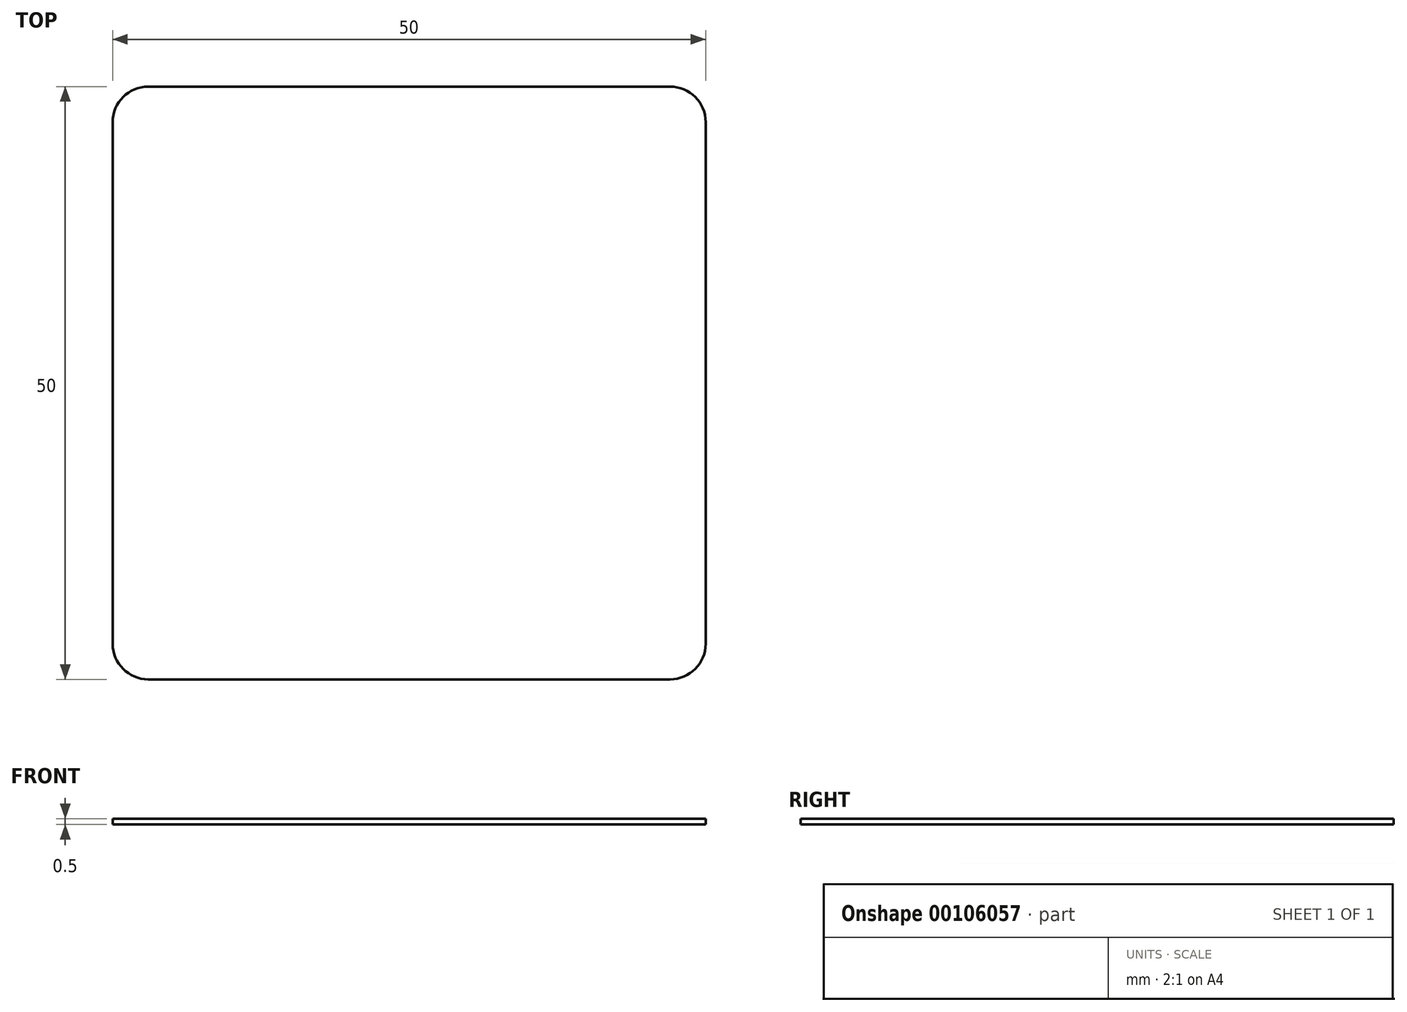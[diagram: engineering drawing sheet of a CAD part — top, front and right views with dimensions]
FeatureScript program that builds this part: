
annotation { "Feature Type Name" : "Feature", "Feature Type Description" : "" }
export const myFeature = defineFeature(function(context is Context, id is Id, definition is map)
    precondition{}
    {
        {
            var Q0;
            Q0=qCreatedBy(makeId("Top.planeOp"),FACE);
            var sketch = newSketch(context, id + "F0", { "sketchPlane" : qUnion([Q0])});
            skLineSegment(sketch, "E0.bottom", {"start": v(3, 0) * mm, "end": v(47, 0) * mm});
            skLineSegment(sketch, "E0.top", {"start": v(3, 50) * mm, "end": v(47, 50) * mm});
            skLineSegment(sketch, "E0.left", {"start": v(0, 3) * mm, "end": v(0, 47) * mm});
            skLineSegment(sketch, "E0.right", {"start": v(50, 3) * mm, "end": v(50, 47) * mm});
            skPoint(sketch, "E1.visualSharp", {"position": v(0, 50) * mm});
            skArc(sketch, "E1.filletArc", {"start": v(3, 50) * mm, "mid": v(0.88, 49.12) * mm, "end": v(0, 47) * mm});
            skPoint(sketch, "E2.visualSharp", {"position": v(50, 50) * mm});
            skArc(sketch, "E2.filletArc", {"start": v(50, 47) * mm, "mid": v(49.12, 49.12) * mm, "end": v(47, 50) * mm});
            skPoint(sketch, "E3.visualSharp", {"position": v(50, 0) * mm});
            skArc(sketch, "E3.filletArc", {"start": v(47, 0) * mm, "mid": v(49.12, 0.88) * mm, "end": v(50, 3) * mm});
            skPoint(sketch, "E4.visualSharp", {"position": v(0, 0) * mm});
            skArc(sketch, "E4.filletArc", {"start": v(0, 3) * mm, "mid": v(0.88, 0.88) * mm, "end": v(3, 0) * mm});
            skSolve(sketch);
        }
        {
            var Q0;
            Q0 = qSketchRegion(id + "F0", true);
            extrude(context, id + "F1", {"entities" : qUnion([Q0]), "depth" : 0.5 * mm});
        }
    });
